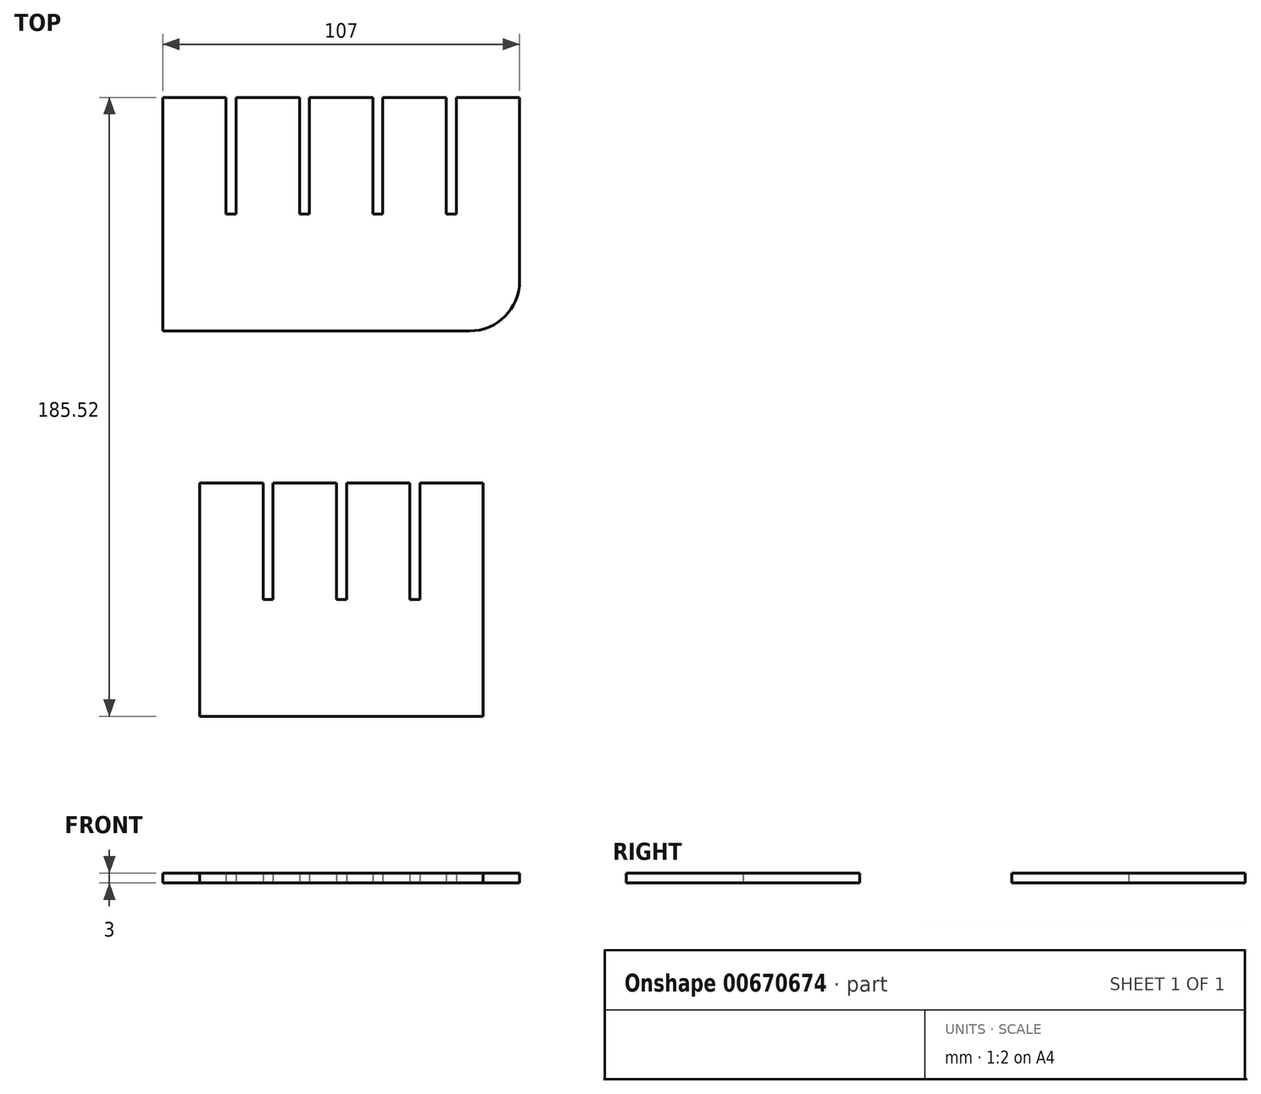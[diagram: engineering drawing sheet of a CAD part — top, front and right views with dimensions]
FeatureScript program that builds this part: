
annotation { "Feature Type Name" : "Feature", "Feature Type Description" : "" }
export const myFeature = defineFeature(function(context is Context, id is Id, definition is map)
    precondition{}
    {
        {
            var Q0;
            Q0=qCreatedBy(makeId("Top.planeOp"),FACE);
            var sketch = newSketch(context, id + "F0", { "sketchPlane" : qUnion([Q0])});
            skLineSegment(sketch, "E0.bottom", {"start": v(-241.45, 62.36) * mm, "end": v(-222.45, 62.36) * mm});
            skLineSegment(sketch, "E0.top", {"start": v(-241.45, -7.64) * mm, "end": v(-156.45, -7.64) * mm});
            skLineSegment(sketch, "E0.left", {"start": v(-241.45, 62.36) * mm, "end": v(-241.45, -7.64) * mm});
            skLineSegment(sketch, "E1.top", {"start": v(-222.45, 27.36) * mm, "end": v(-219.45, 27.36) * mm});
            skLineSegment(sketch, "E1.left", {"start": v(-222.45, 62.36) * mm, "end": v(-222.45, 27.36) * mm});
            skLineSegment(sketch, "E1.right", {"start": v(-219.45, 62.36) * mm, "end": v(-219.45, 27.36) * mm});
            skLineSegment(sketch, "E2.top", {"start": v(-200.45, 27.36) * mm, "end": v(-197.45, 27.36) * mm});
            skLineSegment(sketch, "E2.left", {"start": v(-200.45, 62.36) * mm, "end": v(-200.45, 27.36) * mm});
            skLineSegment(sketch, "E2.right", {"start": v(-197.45, 62.36) * mm, "end": v(-197.45, 27.36) * mm});
            skLineSegment(sketch, "E3.top", {"start": v(-178.45, 27.36) * mm, "end": v(-175.45, 27.36) * mm});
            skLineSegment(sketch, "E3.left", {"start": v(-178.45, 62.36) * mm, "end": v(-178.45, 27.36) * mm});
            skLineSegment(sketch, "E3.right", {"start": v(-175.45, 62.36) * mm, "end": v(-175.45, 27.36) * mm});
            skLineSegment(sketch, "E4.trimOffspring", {"start": v(-197.45, 62.36) * mm, "end": v(-178.45, 62.36) * mm});
            skLineSegment(sketch, "E5.trimOffspring", {"start": v(-219.45, 62.36) * mm, "end": v(-200.45, 62.36) * mm});
            skLineSegment(sketch, "E6.trimOffspring", {"start": v(-175.45, 62.36) * mm, "end": v(-156.45, 62.36) * mm});
            skLineSegment(sketch, "E7.bottom", {"start": v(-252.53, 177.88) * mm, "end": v(-233.53, 177.88) * mm});
            skLineSegment(sketch, "E7.top", {"start": v(-252.53, 107.88) * mm, "end": v(-160.53, 107.88) * mm});
            skLineSegment(sketch, "E7.left", {"start": v(-252.53, 177.88) * mm, "end": v(-252.53, 107.88) * mm});
            skLineSegment(sketch, "E7.right", {"start": v(-145.53, 177.88) * mm, "end": v(-145.53, 122.88) * mm});
            skLineSegment(sketch, "E8.top", {"start": v(-233.53, 142.88) * mm, "end": v(-230.53, 142.88) * mm});
            skLineSegment(sketch, "E8.left", {"start": v(-233.53, 177.88) * mm, "end": v(-233.53, 142.88) * mm});
            skLineSegment(sketch, "E8.right", {"start": v(-230.53, 177.88) * mm, "end": v(-230.53, 142.88) * mm});
            skLineSegment(sketch, "E9.top", {"start": v(-211.53, 142.88) * mm, "end": v(-208.53, 142.88) * mm});
            skLineSegment(sketch, "E9.left", {"start": v(-211.53, 177.88) * mm, "end": v(-211.53, 142.88) * mm});
            skLineSegment(sketch, "E9.right", {"start": v(-208.53, 177.88) * mm, "end": v(-208.53, 142.88) * mm});
            skLineSegment(sketch, "E10.top", {"start": v(-189.53, 142.88) * mm, "end": v(-186.53, 142.88) * mm});
            skLineSegment(sketch, "E10.left", {"start": v(-189.53, 177.88) * mm, "end": v(-189.53, 142.88) * mm});
            skLineSegment(sketch, "E10.right", {"start": v(-186.53, 177.88) * mm, "end": v(-186.53, 142.88) * mm});
            skLineSegment(sketch, "E11.top", {"start": v(-167.53, 142.88) * mm, "end": v(-164.53, 142.88) * mm});
            skLineSegment(sketch, "E11.left", {"start": v(-167.53, 177.88) * mm, "end": v(-167.53, 142.88) * mm});
            skLineSegment(sketch, "E11.right", {"start": v(-164.53, 177.88) * mm, "end": v(-164.53, 142.88) * mm});
            skLineSegment(sketch, "E12.trimOffspring", {"start": v(-208.53, 177.88) * mm, "end": v(-189.53, 177.88) * mm});
            skLineSegment(sketch, "E13.trimOffspring", {"start": v(-230.53, 177.88) * mm, "end": v(-211.53, 177.88) * mm});
            skLineSegment(sketch, "E14.trimOffspring", {"start": v(-186.53, 177.88) * mm, "end": v(-167.53, 177.88) * mm});
            skLineSegment(sketch, "E15.trimOffspring", {"start": v(-164.53, 177.88) * mm, "end": v(-145.53, 177.88) * mm});
            skPoint(sketch, "E16.visualSharp", {"position": v(-145.53, 107.88) * mm});
            skArc(sketch, "E16.filletArc", {"start": v(-160.53, 107.88) * mm, "mid": v(-149.93, 112.28) * mm, "end": v(-145.53, 122.88) * mm});
            skLineSegment(sketch, "E17", {"start": v(-156.45, 62.36) * mm, "end": v(-156.45, -7.64) * mm});
            skSolve(sketch);
        }
        {
            var Q0;
            Q0=makeQuery(id+"F0.imprint","IMPRINT",FACE,{"disambiguationData":[TD([[makeQuery(id+"F0.imprint","IMPRINT",EDGE,{"derivedFrom":sQuery(id+"F0.wireOp",EDGE,"E7.bottom")}),-1.0]])]});
            var Q1;
            Q1=makeQuery(id+"F0.imprint","IMPRINT",FACE,{"disambiguationData":[TD([[makeQuery(id+"F0.imprint","IMPRINT",EDGE,{"derivedFrom":sQuery(id+"F0.wireOp",EDGE,"E0.bottom")}),-1.0]])]});
            extrude(context, id + "F1", {"entities" : qUnion([Q0, Q1]), "depth" : 3 * mm, "offsetDistance" : 25 * mm});
        }
    });
